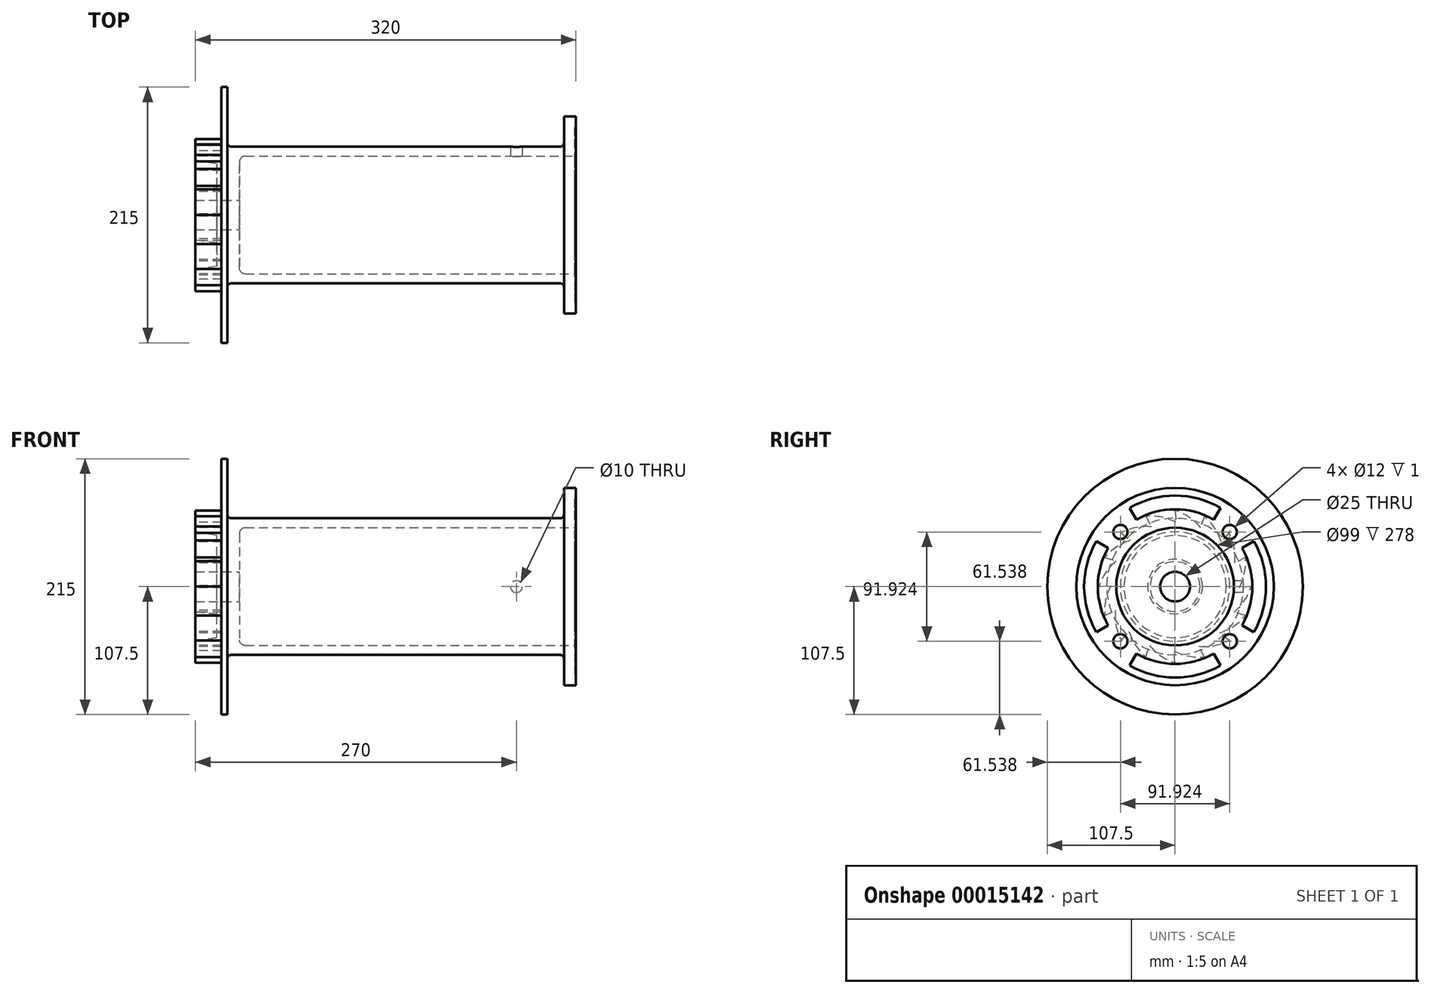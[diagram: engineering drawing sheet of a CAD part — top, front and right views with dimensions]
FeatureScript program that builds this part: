
annotation { "Feature Type Name" : "Feature", "Feature Type Description" : "" }
export const myFeature = defineFeature(function(context is Context, id is Id, definition is map)
    precondition{}
    {
        {
            var Q0;
            Q0=qCreatedBy(makeId("Front.planeOp"),FACE);
            var sketch = newSketch(context, id + "F0", { "sketchPlane" : qUnion([Q0])});
            skLineSegment(sketch, "E0", {"start": v(268.68, 0) * mm, "end": v(-193.18, 0) * mm, "construction": true});
            skLineSegment(sketch, "E1.bottom", {"start": v(0, 49.5) * mm, "end": v(273, 49.5) * mm});
            skLineSegment(sketch, "E1.top", {"start": v(-10, 57.5) * mm, "end": v(273, 57.5) * mm});
            skLineSegment(sketch, "E2.bottom", {"start": v(273, 49.5) * mm, "end": v(283, 49.5) * mm});
            skLineSegment(sketch, "E2.top", {"start": v(273, 83) * mm, "end": v(283, 83) * mm});
            skLineSegment(sketch, "E2.left", {"start": v(273, 57.5) * mm, "end": v(273, 83) * mm});
            skLineSegment(sketch, "E2.right", {"start": v(283, 49.5) * mm, "end": v(283, 83) * mm});
            skLineSegment(sketch, "E3.top", {"start": v(-10, 107.5) * mm, "end": v(-15, 107.5) * mm});
            skLineSegment(sketch, "E3.left", {"start": v(-10, 57.5) * mm, "end": v(-10, 107.5) * mm});
            skLineSegment(sketch, "E3.right", {"start": v(-15, 64) * mm, "end": v(-15, 107.5) * mm});
            skLineSegment(sketch, "E4.top", {"start": v(0, 12.5) * mm, "end": v(-37, 12.5) * mm});
            skLineSegment(sketch, "E4.left", {"start": v(0, 49.5) * mm, "end": v(0, 12.5) * mm});
            skLineSegment(sketch, "E4.right", {"start": v(-37, 21) * mm, "end": v(-37, 12.5) * mm});
            skLineSegment(sketch, "E5", {"start": v(-37, 46) * mm, "end": v(-37, 64) * mm});
            skLineSegment(sketch, "E6", {"start": v(-37, 64) * mm, "end": v(-15, 64) * mm});
            skLineSegment(sketch, "E7", {"start": v(-19, 23) * mm, "end": v(-19, 43) * mm});
            skLineSegment(sketch, "E8", {"start": v(-19, 43) * mm, "end": v(-37, 46) * mm});
            skLineSegment(sketch, "E9", {"start": v(-19, 23) * mm, "end": v(-37, 21) * mm});
            skPoint(sketch, "E10.start.orphan", {"position": v(-37, 29.5) * mm});
            skSolve(sketch);
        }
        {
            var Q0;
            Q0=makeQuery(id+"F0.imprint","IMPRINT",FACE,{"disambiguationData":[TD([[makeQuery(id+"F0.imprint","IMPRINT",EDGE,{"derivedFrom":sQuery(id+"F0.wireOp",EDGE,"E1.bottom")}),1.0]])]});
            var Q1;
            Q1=sQuery(id+"F0.wireOp",EDGE,"E0");
            revolve(context, id + "F1", {"entities" : qUnion([Q0]), "axis" : qUnion([Q1]), "revolveType" : RevolveType.FULL});
        }
        {
            var Q0;
            Q0=makeQuery(id+"F1.opRevolve","SWEPT_FACE",FACE,{"disambiguationData":[OSD([sQuery(id+"F0.wireOp",EDGE,"E2.right")])]});
            var sketch = newSketch(context, id + "F2", { "sketchPlane" : qUnion([Q0])});
            skLineSegment(sketch, "E11", {"start": v(0, 0) * mm, "end": v(158.22, 0) * mm, "construction": true});
            skLineSegment(sketch, "E12", {"start": v(66.25, 38.25) * mm, "end": v(56.3, 32.5) * mm});
            skLineSegment(sketch, "E13", {"start": v(56.3, -32.5) * mm, "end": v(66.25, -38.25) * mm});
            skLineSegment(sketch, "E14", {"start": v(0, 0) * mm, "end": v(106.12, 106.12) * mm, "construction": true});
            skArc(sketch, "E15", {"start": v(38.25, 66.25) * mm, "mid": v(0, 76.5) * mm, "end": v(-38.25, 66.25) * mm});
            skCircle(sketch, "E16", {"center": v(45.96, 45.96) * mm, "radius": 6 * mm});
            skCircle(sketch, "E17.1.0", {"center": v(-45.96, 45.96) * mm, "radius": 6 * mm});
            skCircle(sketch, "E17.2.0", {"center": v(-45.96, -45.96) * mm, "radius": 6 * mm});
            skCircle(sketch, "E17.3.0", {"center": v(45.96, -45.96) * mm, "radius": 6 * mm});
            skLineSegment(sketch, "E18.1.0", {"start": v(-38.25, 66.25) * mm, "end": v(-32.5, 56.3) * mm});
            skLineSegment(sketch, "E18.1.1", {"start": v(32.5, 56.3) * mm, "end": v(38.25, 66.25) * mm});
            skLineSegment(sketch, "E18.2.0", {"start": v(-66.25, -38.25) * mm, "end": v(-56.3, -32.5) * mm});
            skLineSegment(sketch, "E18.2.1", {"start": v(-56.3, 32.5) * mm, "end": v(-66.25, 38.25) * mm});
            skLineSegment(sketch, "E18.3.0", {"start": v(38.25, -66.25) * mm, "end": v(32.5, -56.3) * mm});
            skLineSegment(sketch, "E18.3.1", {"start": v(-32.5, -56.3) * mm, "end": v(-38.25, -66.25) * mm});
            skArc(sketch, "E19.trimOffspring", {"start": v(32.5, 56.3) * mm, "mid": v(0, 65) * mm, "end": v(-32.5, 56.3) * mm});
            skArc(sketch, "E20.trimOffspring", {"start": v(-56.3, 32.5) * mm, "mid": v(-65, 0) * mm, "end": v(-56.3, -32.5) * mm});
            skArc(sketch, "E21.trimOffspring", {"start": v(-66.25, 38.25) * mm, "mid": v(-76.5, 0) * mm, "end": v(-66.25, -38.25) * mm});
            skArc(sketch, "E22.trimOffspring", {"start": v(-38.25, -66.25) * mm, "mid": v(0, -76.5) * mm, "end": v(38.25, -66.25) * mm});
            skArc(sketch, "E23.trimOffspring", {"start": v(66.25, -38.25) * mm, "mid": v(76.5, 0) * mm, "end": v(66.25, 38.25) * mm});
            skArc(sketch, "E24.trimOffspring", {"start": v(-32.5, -56.3) * mm, "mid": v(0, -65) * mm, "end": v(32.5, -56.3) * mm});
            skArc(sketch, "E25.trimOffspring", {"start": v(56.3, -32.5) * mm, "mid": v(65, 0) * mm, "end": v(56.3, 32.5) * mm});
            skSolve(sketch);
        }
        {
            var Q0;
            Q0=makeQuery(id+"F2.imprint","IMPRINT",FACE,{"disambiguationData":[TD([[makeQuery(id+"F2.imprint","IMPRINT",EDGE,{"derivedFrom":sQuery(id+"F2.wireOp",EDGE,"E15")}),1.0]])]});
            var Q1;
            Q1=makeQuery(id+"F2.imprint","IMPRINT",FACE,{"disambiguationData":[TD([[makeQuery(id+"F2.imprint","IMPRINT",EDGE,{"derivedFrom":sQuery(id+"F2.wireOp",EDGE,"E17.1.0")}),1.0]])]});
            var Q2;
            Q2=makeQuery(id+"F2.imprint","IMPRINT",FACE,{"disambiguationData":[TD([[makeQuery(id+"F2.imprint","IMPRINT",EDGE,{"derivedFrom":sQuery(id+"F2.wireOp",EDGE,"E18.2.0")}),1.0]])]});
            var Q3;
            Q3=makeQuery(id+"F2.imprint","IMPRINT",FACE,{"disambiguationData":[TD([[makeQuery(id+"F2.imprint","IMPRINT",EDGE,{"derivedFrom":sQuery(id+"F2.wireOp",EDGE,"E17.2.0")}),1.0]])]});
            var Q4;
            Q4=makeQuery(id+"F2.imprint","IMPRINT",FACE,{"disambiguationData":[TD([[makeQuery(id+"F2.imprint","IMPRINT",EDGE,{"derivedFrom":sQuery(id+"F2.wireOp",EDGE,"E18.3.0")}),1.0]])]});
            var Q5;
            Q5=makeQuery(id+"F2.imprint","IMPRINT",FACE,{"disambiguationData":[TD([[makeQuery(id+"F2.imprint","IMPRINT",EDGE,{"derivedFrom":sQuery(id+"F2.wireOp",EDGE,"E17.3.0")}),1.0]])]});
            var Q6;
            Q6=makeQuery(id+"F2.imprint","IMPRINT",FACE,{"disambiguationData":[TD([[makeQuery(id+"F2.imprint","IMPRINT",EDGE,{"derivedFrom":sQuery(id+"F2.wireOp",EDGE,"E12")}),1.0]])]});
            var Q7;
            Q7=makeQuery(id+"F2.imprint","IMPRINT",FACE,{"disambiguationData":[TD([[makeQuery(id+"F2.imprint","IMPRINT",EDGE,{"derivedFrom":sQuery(id+"F2.wireOp",EDGE,"E16")}),1.0]])]});
            extrude(context, id + "F3", {"entities" : qUnion([Q0, Q1, Q2, Q3, Q4, Q5, Q6, Q7]), "operationType" : NewBodyOperationType.REMOVE, "oppositeDirection" : true, "depth" : 1 * mm});
        }
        {
            var Q0;
            Q0=makeQuery(id+"F1.opRevolve","SWEPT_EDGE",EDGE,{"disambiguationData":[OSD([sQuery(id+"F0.wireOp",EDGE,"E1.bottom"),sQuery(id+"F0.wireOp",EDGE,"E4.left")])]});
            fillet(context, id + "F4", {"entities" : qUnion([Q0]), "radius" : 5 * mm, "tangentPropagation" : true, "allowEdgeOverflow" : false});
        }
        {
            var Q0;
            Q0=makeQuery(id+"F1.opRevolve","SWEPT_EDGE",EDGE,{"disambiguationData":[OSD([sQuery(id+"F0.wireOp",EDGE,"E1.top"),sQuery(id+"F0.wireOp",EDGE,"E3.left")])]});
            var Q1;
            Q1=makeQuery(id+"F1.opRevolve","SWEPT_EDGE",EDGE,{"disambiguationData":[OSD([sQuery(id+"F0.wireOp",EDGE,"E1.top"),sQuery(id+"F0.wireOp",EDGE,"E2.left")])]});
            fillet(context, id + "F5", {"entities" : qUnion([Q0, Q1]), "radius" : 3 * mm, "tangentPropagation" : true, "allowEdgeOverflow" : false});
        }
        {
            var Q0;
            Q0=makeQuery(id+"F1.opRevolve","SWEPT_FACE",FACE,{"disambiguationData":[OSD([sQuery(id+"F0.wireOp",EDGE,"E5")])]});
            var sketch = newSketch(context, id + "F6", { "sketchPlane" : qUnion([Q0])});
            skLineSegment(sketch, "E26", {"start": v(0, 0) * mm, "end": v(0, 92.53) * mm, "construction": true});
            skLineSegment(sketch, "E27", {"start": v(0, 0) * mm, "end": v(-93.52, 0) * mm, "construction": true});
            skArc(sketch, "E28.0", {"start": v(-49.89, 20.66) * mm, "mid": v(-53.05, 10.1) * mm, "end": v(-54, -0.88) * mm});
            skLineSegment(sketch, "E29", {"start": v(0, 0) * mm, "end": v(-81.13, 33.6) * mm, "construction": true});
            skLineSegment(sketch, "E30", {"start": v(-59.13, 24.5) * mm, "end": v(-50.22, 19.85) * mm});
            skLineSegment(sketch, "E31", {"start": v(-64, 0) * mm, "end": v(-54, -0.88) * mm});
            skArc(sketch, "E32", {"start": v(-59.13, 24.5) * mm, "mid": v(-58.42, 11.43) * mm, "end": v(-54, -0.88) * mm});
            skArc(sketch, "E33.1.0", {"start": v(-64, 0) * mm, "mid": v(-58.35, -11.8) * mm, "end": v(-49.55, -21.47) * mm});
            skArc(sketch, "E33.1.2", {"start": v(-54, 0) * mm, "mid": v(-52.88, -10.96) * mm, "end": v(-49.55, -21.47) * mm});
            skArc(sketch, "E33.2.0", {"start": v(-59.13, -24.5) * mm, "mid": v(-49.4, -33.23) * mm, "end": v(-37.56, -38.8) * mm});
            skLineSegment(sketch, "E33.2.1", {"start": v(-59.13, -24.5) * mm, "end": v(-49.55, -21.47) * mm});
            skArc(sketch, "E33.2.2", {"start": v(-49.89, -20.66) * mm, "mid": v(-44.65, -30.36) * mm, "end": v(-37.56, -38.8) * mm});
            skArc(sketch, "E33.3.0", {"start": v(-45.25, -45.25) * mm, "mid": v(-32.92, -49.6) * mm, "end": v(-19.85, -50.22) * mm});
            skLineSegment(sketch, "E33.3.1", {"start": v(-45.25, -45.25) * mm, "end": v(-37.56, -38.8) * mm});
            skArc(sketch, "E33.3.2", {"start": v(-38.18, -38.18) * mm, "mid": v(-29.64, -45.14) * mm, "end": v(-19.85, -50.22) * mm});
            skArc(sketch, "E33.4.0", {"start": v(-24.5, -59.13) * mm, "mid": v(-11.43, -58.42) * mm, "end": v(0.88, -54) * mm});
            skLineSegment(sketch, "E33.4.1", {"start": v(-24.5, -59.13) * mm, "end": v(-19.85, -50.22) * mm});
            skArc(sketch, "E33.4.2", {"start": v(-20.66, -49.89) * mm, "mid": v(-10.1, -53.05) * mm, "end": v(0.88, -54) * mm});
            skArc(sketch, "E33.5.0", {"start": v(0, -64) * mm, "mid": v(11.8, -58.35) * mm, "end": v(21.47, -49.55) * mm});
            skLineSegment(sketch, "E33.5.1", {"start": v(0, -64) * mm, "end": v(0.88, -54) * mm});
            skArc(sketch, "E33.5.2", {"start": v(0, -54) * mm, "mid": v(10.96, -52.88) * mm, "end": v(21.47, -49.55) * mm});
            skArc(sketch, "E33.6.0", {"start": v(24.5, -59.13) * mm, "mid": v(33.23, -49.4) * mm, "end": v(38.8, -37.56) * mm});
            skLineSegment(sketch, "E33.6.1", {"start": v(24.5, -59.13) * mm, "end": v(21.47, -49.55) * mm});
            skArc(sketch, "E33.6.2", {"start": v(20.66, -49.89) * mm, "mid": v(30.36, -44.65) * mm, "end": v(38.8, -37.56) * mm});
            skArc(sketch, "E33.7.0", {"start": v(45.25, -45.25) * mm, "mid": v(49.6, -32.92) * mm, "end": v(50.22, -19.85) * mm});
            skLineSegment(sketch, "E33.7.1", {"start": v(45.25, -45.25) * mm, "end": v(38.8, -37.56) * mm});
            skArc(sketch, "E33.7.2", {"start": v(38.18, -38.18) * mm, "mid": v(45.14, -29.64) * mm, "end": v(50.22, -19.85) * mm});
            skArc(sketch, "E33.8.0", {"start": v(59.13, -24.5) * mm, "mid": v(58.42, -11.43) * mm, "end": v(54, 0.88) * mm});
            skLineSegment(sketch, "E33.8.1", {"start": v(59.13, -24.5) * mm, "end": v(50.22, -19.85) * mm});
            skArc(sketch, "E33.8.2", {"start": v(49.89, -20.66) * mm, "mid": v(53.05, -10.1) * mm, "end": v(54, 0.88) * mm});
            skArc(sketch, "E33.9.0", {"start": v(64, 0) * mm, "mid": v(58.35, 11.8) * mm, "end": v(49.55, 21.47) * mm});
            skLineSegment(sketch, "E33.9.1", {"start": v(64, 0) * mm, "end": v(54, 0.88) * mm});
            skArc(sketch, "E33.9.2", {"start": v(54, 0) * mm, "mid": v(52.88, 10.96) * mm, "end": v(49.55, 21.47) * mm});
            skArc(sketch, "E33.10.0", {"start": v(59.13, 24.5) * mm, "mid": v(49.4, 33.23) * mm, "end": v(37.56, 38.8) * mm});
            skLineSegment(sketch, "E33.10.1", {"start": v(59.13, 24.5) * mm, "end": v(49.55, 21.47) * mm});
            skArc(sketch, "E33.10.2", {"start": v(49.89, 20.66) * mm, "mid": v(44.65, 30.36) * mm, "end": v(37.56, 38.8) * mm});
            skArc(sketch, "E33.11.0", {"start": v(45.25, 45.25) * mm, "mid": v(32.92, 49.6) * mm, "end": v(19.85, 50.22) * mm});
            skLineSegment(sketch, "E33.11.1", {"start": v(45.25, 45.25) * mm, "end": v(37.56, 38.8) * mm});
            skArc(sketch, "E33.11.2", {"start": v(38.18, 38.18) * mm, "mid": v(29.64, 45.14) * mm, "end": v(19.85, 50.22) * mm});
            skArc(sketch, "E33.12.0", {"start": v(24.5, 59.13) * mm, "mid": v(11.43, 58.42) * mm, "end": v(-0.88, 54) * mm});
            skLineSegment(sketch, "E33.12.1", {"start": v(24.5, 59.13) * mm, "end": v(19.85, 50.22) * mm});
            skArc(sketch, "E33.12.2", {"start": v(20.66, 49.89) * mm, "mid": v(10.1, 53.05) * mm, "end": v(-0.88, 54) * mm});
            skArc(sketch, "E33.13.0", {"start": v(0, 64) * mm, "mid": v(-11.8, 58.35) * mm, "end": v(-21.47, 49.55) * mm});
            skLineSegment(sketch, "E33.13.1", {"start": v(0, 64) * mm, "end": v(-0.88, 54) * mm});
            skArc(sketch, "E33.13.2", {"start": v(0, 54) * mm, "mid": v(-10.96, 52.88) * mm, "end": v(-21.47, 49.55) * mm});
            skArc(sketch, "E33.14.0", {"start": v(-24.5, 59.13) * mm, "mid": v(-33.23, 49.4) * mm, "end": v(-38.8, 37.56) * mm});
            skLineSegment(sketch, "E33.14.1", {"start": v(-24.5, 59.13) * mm, "end": v(-21.47, 49.55) * mm});
            skArc(sketch, "E33.14.2", {"start": v(-20.66, 49.89) * mm, "mid": v(-30.36, 44.65) * mm, "end": v(-38.8, 37.56) * mm});
            skArc(sketch, "E33.15.0", {"start": v(-45.25, 45.25) * mm, "mid": v(-49.6, 32.92) * mm, "end": v(-50.22, 19.85) * mm});
            skLineSegment(sketch, "E33.15.1", {"start": v(-45.25, 45.25) * mm, "end": v(-38.8, 37.56) * mm});
            skArc(sketch, "E33.15.2", {"start": v(-38.18, 38.18) * mm, "mid": v(-45.14, 29.64) * mm, "end": v(-50.22, 19.85) * mm});
            skSolve(sketch);
        }
        {
            var Q0;
            {var subQ2=sQuery(id+"F6.wireOp",EDGE,"E30");Q0=makeQuery(id+"F6.imprint","IMPRINT",FACE,{"disambiguationData":[TD([[makeQuery(id+"F6.imprint","IMPRINT",EDGE,{"derivedFrom":subQ2}),1.0]])]});}
            var Q1;
            {var subQ2=sQuery(id+"F6.wireOp",EDGE,"E33.14.0");Q1=makeQuery(id+"F6.imprint","IMPRINT",FACE,{"disambiguationData":[TD([[makeQuery(id+"F6.imprint","IMPRINT",EDGE,{"derivedFrom":subQ2}),-1.0]])]});}
            var Q2;
            {var subQ2=sQuery(id+"F6.wireOp",EDGE,"E33.13.0");Q2=makeQuery(id+"F6.imprint","IMPRINT",FACE,{"disambiguationData":[TD([[makeQuery(id+"F6.imprint","IMPRINT",EDGE,{"derivedFrom":subQ2}),-1.0]])]});}
            var Q3;
            {var subQ2=sQuery(id+"F6.wireOp",EDGE,"E33.12.0");Q3=makeQuery(id+"F6.imprint","IMPRINT",FACE,{"disambiguationData":[TD([[makeQuery(id+"F6.imprint","IMPRINT",EDGE,{"derivedFrom":subQ2}),-1.0]])]});}
            var Q4;
            {var subQ2=sQuery(id+"F6.wireOp",EDGE,"E33.11.0");Q4=makeQuery(id+"F6.imprint","IMPRINT",FACE,{"disambiguationData":[TD([[makeQuery(id+"F6.imprint","IMPRINT",EDGE,{"derivedFrom":subQ2}),-1.0]])]});}
            var Q5;
            {var subQ2=sQuery(id+"F6.wireOp",EDGE,"E33.10.0");Q5=makeQuery(id+"F6.imprint","IMPRINT",FACE,{"disambiguationData":[TD([[makeQuery(id+"F6.imprint","IMPRINT",EDGE,{"derivedFrom":subQ2}),-1.0]])]});}
            var Q6;
            {var subQ2=sQuery(id+"F6.wireOp",EDGE,"E33.9.0");Q6=makeQuery(id+"F6.imprint","IMPRINT",FACE,{"disambiguationData":[TD([[makeQuery(id+"F6.imprint","IMPRINT",EDGE,{"derivedFrom":subQ2}),-1.0]])]});}
            var Q7;
            {var subQ2=sQuery(id+"F6.wireOp",EDGE,"E33.8.0");Q7=makeQuery(id+"F6.imprint","IMPRINT",FACE,{"disambiguationData":[TD([[makeQuery(id+"F6.imprint","IMPRINT",EDGE,{"derivedFrom":subQ2}),-1.0]])]});}
            var Q8;
            {var subQ2=sQuery(id+"F6.wireOp",EDGE,"E33.7.0");Q8=makeQuery(id+"F6.imprint","IMPRINT",FACE,{"disambiguationData":[TD([[makeQuery(id+"F6.imprint","IMPRINT",EDGE,{"derivedFrom":subQ2}),-1.0]])]});}
            var Q9;
            {var subQ2=sQuery(id+"F6.wireOp",EDGE,"E33.6.0");Q9=makeQuery(id+"F6.imprint","IMPRINT",FACE,{"disambiguationData":[TD([[makeQuery(id+"F6.imprint","IMPRINT",EDGE,{"derivedFrom":subQ2}),-1.0]])]});}
            var Q10;
            {var subQ2=sQuery(id+"F6.wireOp",EDGE,"E33.5.0");Q10=makeQuery(id+"F6.imprint","IMPRINT",FACE,{"disambiguationData":[TD([[makeQuery(id+"F6.imprint","IMPRINT",EDGE,{"derivedFrom":subQ2}),-1.0]])]});}
            var Q11;
            {var subQ2=sQuery(id+"F6.wireOp",EDGE,"E33.4.0");Q11=makeQuery(id+"F6.imprint","IMPRINT",FACE,{"disambiguationData":[TD([[makeQuery(id+"F6.imprint","IMPRINT",EDGE,{"derivedFrom":subQ2}),-1.0]])]});}
            var Q12;
            {var subQ2=sQuery(id+"F6.wireOp",EDGE,"E33.3.0");Q12=makeQuery(id+"F6.imprint","IMPRINT",FACE,{"disambiguationData":[TD([[makeQuery(id+"F6.imprint","IMPRINT",EDGE,{"derivedFrom":subQ2}),-1.0]])]});}
            var Q13;
            {var subQ2=sQuery(id+"F6.wireOp",EDGE,"E33.2.0");Q13=makeQuery(id+"F6.imprint","IMPRINT",FACE,{"disambiguationData":[TD([[makeQuery(id+"F6.imprint","IMPRINT",EDGE,{"derivedFrom":subQ2}),-1.0]])]});}
            var Q14;
            {var subQ2=sQuery(id+"F6.wireOp",EDGE,"E33.1.0");Q14=makeQuery(id+"F6.imprint","IMPRINT",FACE,{"disambiguationData":[TD([[makeQuery(id+"F6.imprint","IMPRINT",EDGE,{"derivedFrom":subQ2}),-1.0]])]});}
            var Q15;
            {var subQ2=sQuery(id+"F6.wireOp",EDGE,"E32");Q15=makeQuery(id+"F6.imprint","IMPRINT",FACE,{"disambiguationData":[TD([[makeQuery(id+"F6.imprint","IMPRINT",EDGE,{"derivedFrom":subQ2}),-1.0]])]});}
            var Q16;
            Q16=makeQuery(id+"F1.opRevolve","SWEPT_FACE",FACE,{"disambiguationData":[OSD([sQuery(id+"F0.wireOp",EDGE,"E3.right")])]});
            extrude(context, id + "F7", {"entities" : qUnion([Q0, Q1, Q2, Q3, Q4, Q5, Q6, Q7, Q8, Q9, Q10, Q11, Q12, Q13, Q14, Q15]), "operationType" : NewBodyOperationType.REMOVE, "endBound" : BoundingType.UP_TO_SURFACE, "oppositeDirection" : true, "endBoundEntityFace" : qUnion([Q16]), "depth" : 25 * mm});
        }
        {
            var Q0;
            Q0=qCreatedBy(makeId("Front.planeOp"),FACE);
            var sketch = newSketch(context, id + "F8", { "sketchPlane" : qUnion([Q0])});
            skCircle(sketch, "E34", {"center": v(233, 0) * mm, "radius": 5 * mm});
            skLineSegment(sketch, "E35.0", {"start": v(283, 83) * mm, "end": v(283, -83) * mm});
            skSolve(sketch);
        }
        {
            var Q0;
            Q0=makeQuery(id+"F8.imprint","IMPRINT",FACE,{"disambiguationData":[TD([[makeQuery(id+"F8.imprint","IMPRINT",EDGE,{"derivedFrom":sQuery(id+"F8.wireOp",EDGE,"E34")}),1.0]])]});
            extrude(context, id + "F9", {"entities" : qUnion([Q0]), "operationType" : NewBodyOperationType.REMOVE, "endBound" : BoundingType.THROUGH_ALL, "oppositeDirection" : true, "depth" : 25 * mm});
        }
    });
